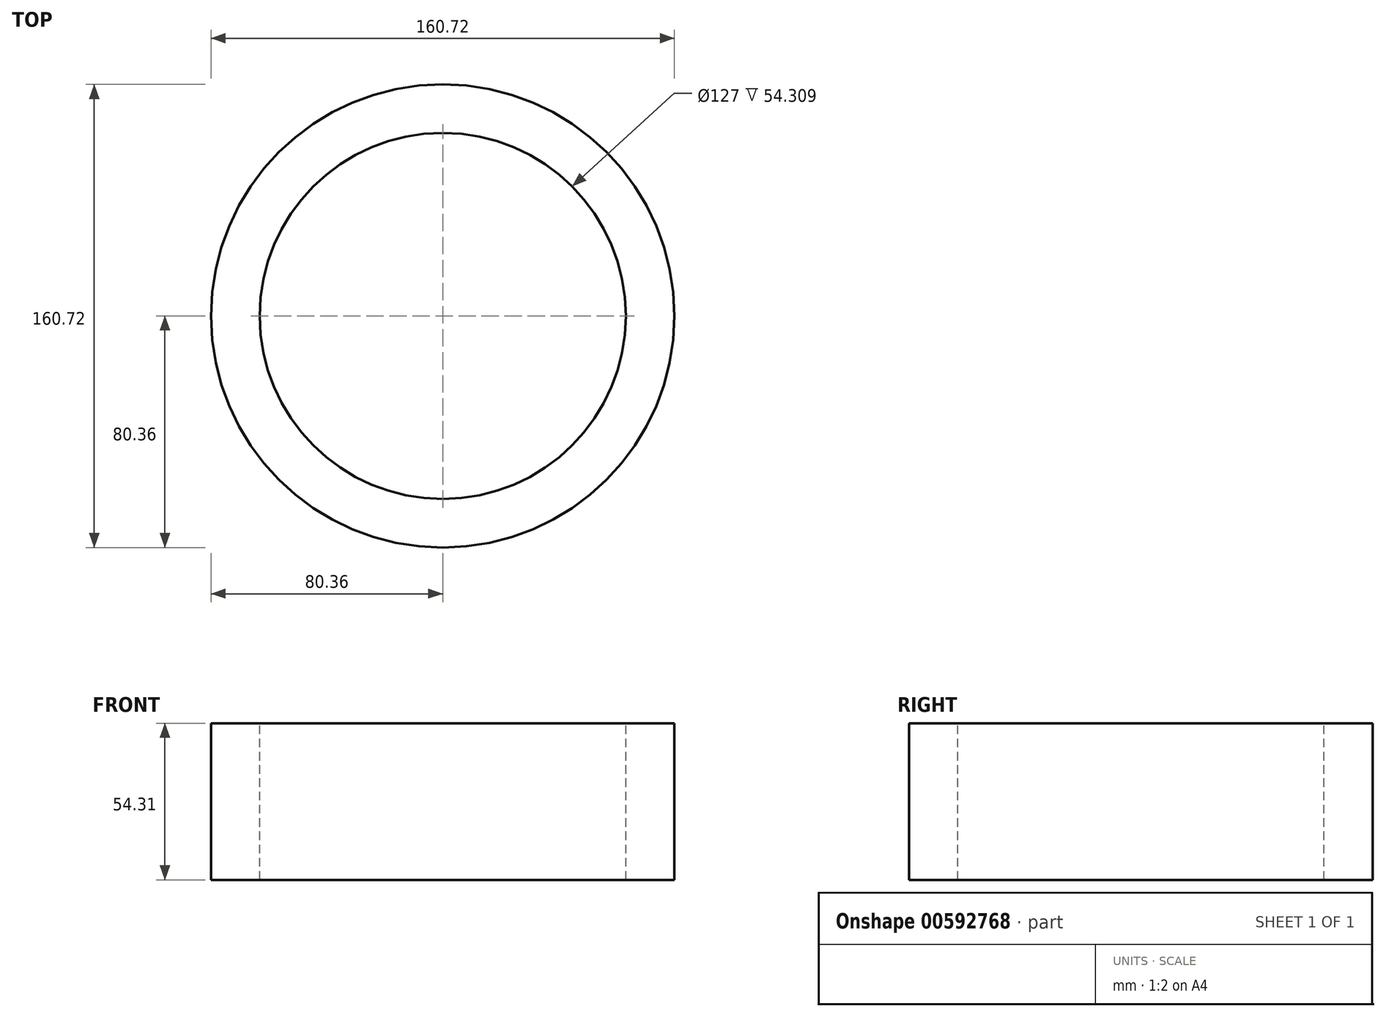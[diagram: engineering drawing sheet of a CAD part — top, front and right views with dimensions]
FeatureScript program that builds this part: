
annotation { "Feature Type Name" : "Feature", "Feature Type Description" : "" }
export const myFeature = defineFeature(function(context is Context, id is Id, definition is map)
    precondition{}
    {
        {
            var Q0;
            Q0=qCreatedBy(makeId("Front.planeOp"),FACE);
            var sketch = newSketch(context, id + "F0", { "sketchPlane" : qUnion([Q0])});
            skLineSegment(sketch, "E0.bottom", {"start": v(0, 0) * mm, "end": v(80.36, 0) * mm});
            skLineSegment(sketch, "E0.top", {"start": v(0, -54.3) * mm, "end": v(80.36, -54.3) * mm});
            skLineSegment(sketch, "E0.left", {"start": v(0, 0) * mm, "end": v(0, -54.3) * mm});
            skLineSegment(sketch, "E0.right", {"start": v(80.36, 0) * mm, "end": v(80.36, -54.3) * mm});
            skSolve(sketch);
        }
        {
            var Q0;
            Q0 = qSketchRegion(id + "F0", true);
            var Q1;
            Q1=sQuery(id+"F0.wireOp",EDGE,"E0.left");
            revolve(context, id + "F1", {"entities" : qUnion([Q0]), "axis" : qUnion([Q1]), "revolveType" : RevolveType.FULL});
        }
        {
            var Q0;
            Q0=makeQuery(id+"F1.opRevolve","SWEPT_FACE",FACE,{"disambiguationData":[OSD([sQuery(id+"F0.wireOp",EDGE,"E0.bottom")])]});
            var sketch = newSketch(context, id + "F2", { "sketchPlane" : qUnion([Q0])});
            skCircle(sketch, "E1", {"center": v(0, 0) * mm, "radius": 63.5 * mm});
            skSolve(sketch);
        }
        {
            var Q0;
            Q0=makeQuery(id+"F2.imprint","IMPRINT",FACE,{"disambiguationData":[TD([[makeQuery(id+"F2.imprint","IMPRINT",EDGE,{"derivedFrom":sQuery(id+"F2.wireOp",EDGE,"E1")}),1.0]])]});
            extrude(context, id + "F3", {"entities" : qUnion([Q0]), "operationType" : NewBodyOperationType.REMOVE, "endBound" : BoundingType.THROUGH_ALL, "oppositeDirection" : true, "depth" : 25.4 * mm, "offsetDistance" : 25.4 * mm});
        }
    });
